# Revit family: Window_Curtain_Wall-Fixed-Traco-NX_3800-Commercial
name_source: partatom
category: Windows
revit_build: Autodesk Revit 2015 (Build: 20140905_0730(x64)
units: mm (PartAtom-declared; Revit-internal decimal feet)

## types (1)
- NX-3800 - Standard
    Allowable Air Infiltration Maximum = 0.1 @ 6.2 PSF
    Assembly Code = B2020110
    Blind Placement = 0' - 1 1/8"
    CTRL Configuration Number = 1
    CTRL Glazing L/R Visibility Offset = 0' - 0"
    CTRL Glazing T/B Visibility Offset = 0' - 0"
    Condensation Resistance = 44.0000 psf
    Depth = 0' - 3 1/4"
    Description = Commercial, Fixed Window
    Designation = AAMA/WDMA/CSA 101/I.S.2/A-440-05: FW-AW90
    Dual Glazing = No
    Dual Glazing Inset = 0' - 0 1/4"
    Forced Entry Resistance = TYPE D: GRADE 10
    Frame Material = Aluminum - Traco - Anodized - Bronze
    Full Glazing = Yes
    Glazing Inset = 0' - 0 1/4"
    Glazing Material = Glass - Traco - Clear
    Glazing Thickness = 0' - 1"
    Head Width = 0' - 2 3/16"
    Height Maximum = 5' - 0"
    Height Minimum = 2' - 6"
    Jamb Width = 0' - 2 3/16"
    Keynote = 08520
    Manufacturer = Traco
    Model = NX-3800
    Product Documentation Link = http://www.alcoa.com
    Product Page URL = http://www.alcoa.com
    Product data url = https://bimobject.com
    Rail Width = 0' - 3 1/4"
    Sill Width = 0' - 2 3/16"
    Test Size = 60" X 99"
    Triple Glazing = No
    Type Comments = Fixed, Standard
    URL = http://www.alcoa.com
    Uniform Load Deflection = 80.0000 psf
    Uniform Load Structural = 120.0000 psf
    Vertical Mullion = No
    Water Resistance = 15.0000 psf
    Width Maximum = 8' - 0"
    Width Minimum = 3' - 0"

## geometry (parser evidence)
native form markers: Blend x2, Sweep x7
no freeform markers — native parametric forms only
